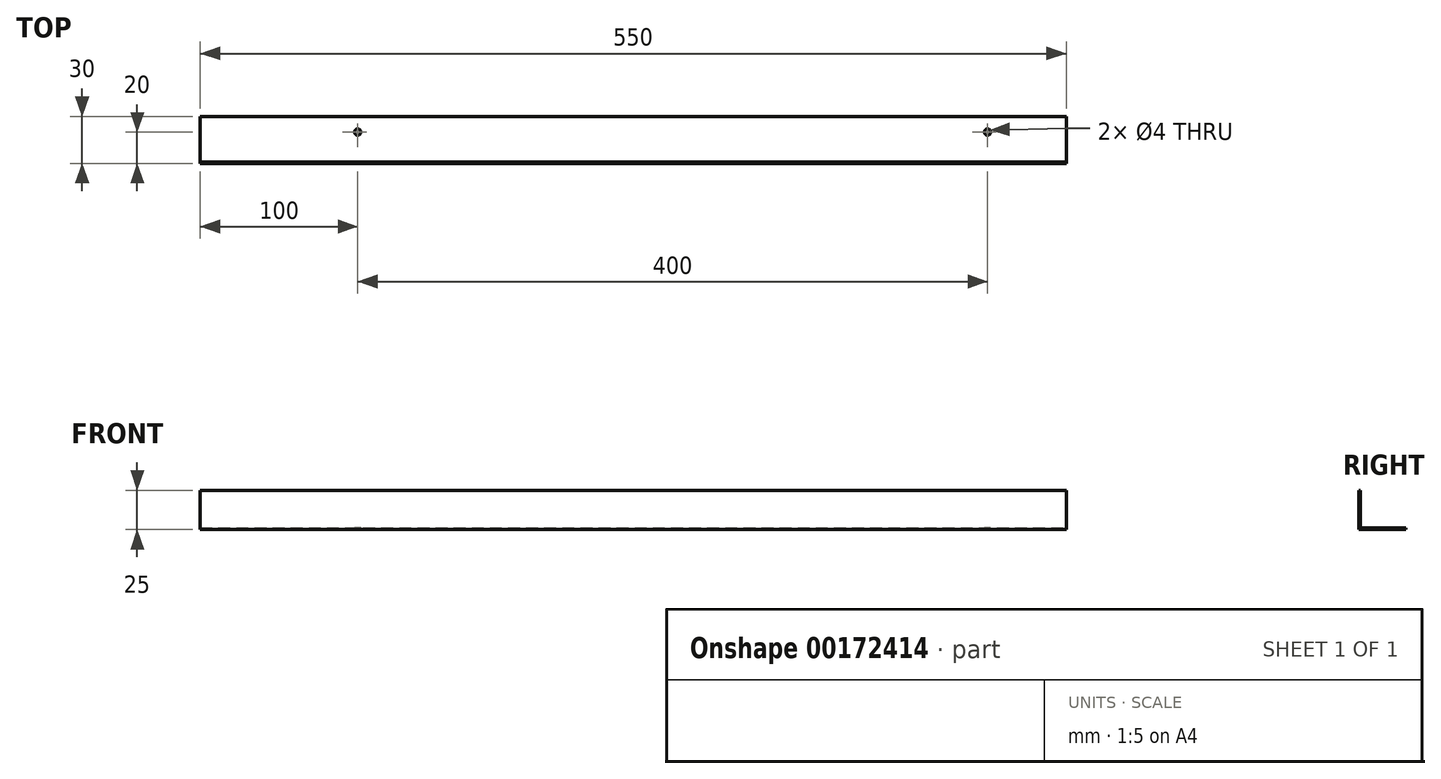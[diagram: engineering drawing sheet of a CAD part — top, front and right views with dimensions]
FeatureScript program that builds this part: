
annotation { "Feature Type Name" : "Feature", "Feature Type Description" : "" }
export const myFeature = defineFeature(function(context is Context, id is Id, definition is map)
    precondition{}
    {
        {
            var Q0;
            Q0=qCreatedBy(makeId("Top.planeOp"),FACE);
            var sketch = newSketch(context, id + "F0", { "sketchPlane" : qUnion([Q0])});
            skLineSegment(sketch, "E0.bottom", {"start": v(0, 0) * mm, "end": v(550, 0) * mm});
            skLineSegment(sketch, "E0.top", {"start": v(0, 30) * mm, "end": v(550, 30) * mm});
            skLineSegment(sketch, "E0.left", {"start": v(0, 0) * mm, "end": v(0, 30) * mm});
            skLineSegment(sketch, "E0.right", {"start": v(550, 0) * mm, "end": v(550, 30) * mm});
            skSolve(sketch);
        }
        {
            var Q0;
            Q0 = qSketchRegion(id + "F0", true);
            extrude(context, id + "F1", {"entities" : qUnion([Q0]), "depth" : 1 * mm});
        }
        {
            var Q0;
            Q0=makeQuery(id+"F1.opExtrude","CAP_FACE",FACE,{"disambiguationData":[OSD([sQuery(id+"F0.wireOp",EDGE,"E0.bottom"),sQuery(id+"F0.wireOp",EDGE,"E0.top"),sQuery(id+"F0.wireOp",EDGE,"E0.left"),sQuery(id+"F0.wireOp",EDGE,"E0.right")])],"isStart":false});
            var sketch = newSketch(context, id + "F2", { "sketchPlane" : qUnion([Q0])});
            skLineSegment(sketch, "E1.bottom", {"start": v(0, 0) * mm, "end": v(550, 0) * mm});
            skLineSegment(sketch, "E1.top", {"start": v(0, 1) * mm, "end": v(550, 1) * mm});
            skLineSegment(sketch, "E1.left", {"start": v(0, 0) * mm, "end": v(0, 1) * mm});
            skLineSegment(sketch, "E1.right", {"start": v(550, 0) * mm, "end": v(550, 1) * mm});
            skSolve(sketch);
        }
        {
            var Q0;
            Q0 = qSketchRegion(id + "F2", true);
            extrude(context, id + "F3", {"entities" : qUnion([Q0]), "operationType" : NewBodyOperationType.ADD, "depth" : 24 * mm});
        }
        {
            var Q0;
            Q0=makeQuery(id+"F1.opExtrude","CAP_FACE",FACE,{"disambiguationData":[OSD([sQuery(id+"F0.wireOp",EDGE,"E0.bottom"),sQuery(id+"F0.wireOp",EDGE,"E0.top"),sQuery(id+"F0.wireOp",EDGE,"E0.left"),sQuery(id+"F0.wireOp",EDGE,"E0.right")])],"isStart":false});
            var sketch = newSketch(context, id + "F4", { "sketchPlane" : qUnion([Q0])});
            skCircle(sketch, "E2", {"center": v(100, 20) * mm, "radius": 2 * mm});
            skCircle(sketch, "E3.1.0.0", {"center": v(500, 20) * mm, "radius": 2 * mm});
            skLineSegment(sketch, "E3.direction1", {"start": v(100, 20) * mm, "end": v(500, 20) * mm, "construction": true});
            skSolve(sketch);
        }
        {
            var Q0;
            Q0 = qSketchRegion(id + "F4", true);
            extrude(context, id + "F5", {"entities" : qUnion([Q0]), "operationType" : NewBodyOperationType.REMOVE, "endBound" : BoundingType.THROUGH_ALL, "oppositeDirection" : true, "depth" : 25 * mm});
        }
    });
